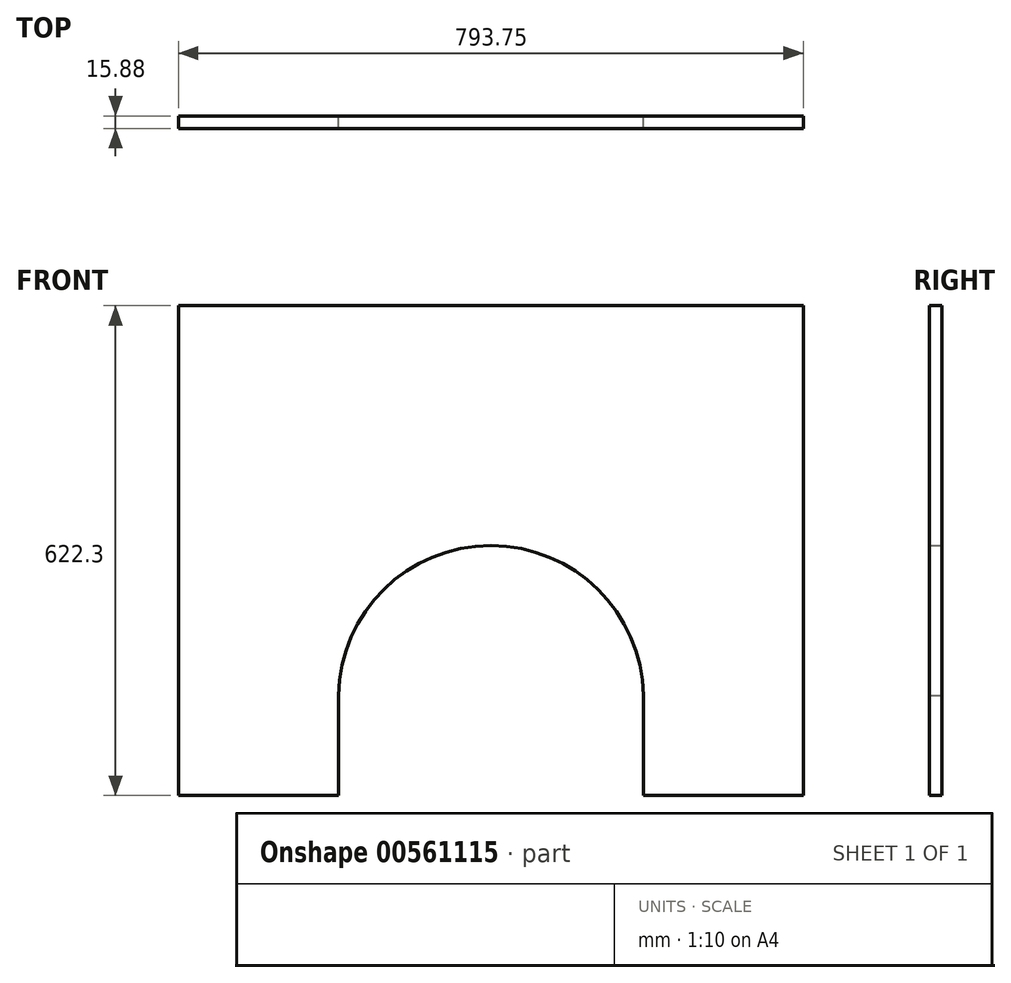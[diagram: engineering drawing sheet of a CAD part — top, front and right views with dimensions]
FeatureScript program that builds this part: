
annotation { "Feature Type Name" : "Feature", "Feature Type Description" : "" }
export const myFeature = defineFeature(function(context is Context, id is Id, definition is map)
    precondition{}
    {
        {
            var Q0;
            Q0=qCreatedBy(makeId("Front.planeOp"),FACE);
            var sketch = newSketch(context, id + "F0", { "sketchPlane" : qUnion([Q0])});
            skLineSegment(sketch, "E0", {"start": v(-32.8, 308.59) * mm, "end": v(760.96, 308.59) * mm});
            skLineSegment(sketch, "E1", {"start": v(760.96, 308.59) * mm, "end": v(760.96, -313.71) * mm});
            skLineSegment(sketch, "E2", {"start": v(760.96, -313.71) * mm, "end": v(557.76, -313.71) * mm});
            skLineSegment(sketch, "E3", {"start": v(-32.8, 308.59) * mm, "end": v(-32.8, -313.71) * mm});
            skLineSegment(sketch, "E4", {"start": v(-32.8, -313.71) * mm, "end": v(170.4, -313.71) * mm});
            skLineSegment(sketch, "E5", {"start": v(170.4, -313.71) * mm, "end": v(170.4, -186.71) * mm});
            skLineSegment(sketch, "E6", {"start": v(557.76, -313.71) * mm, "end": v(557.76, -186.71) * mm});
            skArc(sketch, "E7", {"start": v(557.76, -186.71) * mm, "mid": v(364.08, 3.79) * mm, "end": v(170.4, -186.71) * mm});
            skPoint(sketch, "E8.start.orphan", {"position": v(364.08, 308.59) * mm});
            skSolve(sketch);
        }
        {
            var Q0;
            Q0 = qSketchRegion(id + "F0", true);
            extrude(context, id + "F1", {"entities" : qUnion([Q0]), "depth" : 15.88 * mm, "offsetDistance" : 25.4 * mm});
        }
    });
